# Revit family: Shower-Handshower-KOHLER-Awaken-K-99898
name_source: partatom
category: Plumbing Fixtures
revit_build: Autodesk Revit 2015 (Build: 20140606_1530(x64)
units: mm (PartAtom-declared; Revit-internal decimal feet)

## types (2) — shared parameters
ADA Compliant = Yes
Assembly Code = D2010700
CW Connection = Yes
Date Modified = 09/18/2017
Default Elevation = 42"
Description = G110 premium slidebar kit
Flow Rate = 2 GPM
HW Connection = Yes
Height = 46 9/16"
Length = 8 25/32"
Manufacturer = Kohler
MasterFormat 1995 = 15410
MasterFormat 2004 = 22.41.39
Material = Premium Metal
Pressure = 0.00 psi
Product Documentation Link = http://www.us.kohler.com
Product Name = Awaken
Product Page URL = http://www.us.kohler.com
URL = http://www.us.kohler.com
Width = 4 13/16"

## per-type parameters (varying)
| type | Finish | Model | Type |
| CP-Polished Chrome | Metal-Kohler-CP-Polished Chrome | K-99898-CP | 1 |
| BN-Vibrant Brushed Nickel | Metal-Kohler-BN-Vibrant Brushed Nickel | K-99898-BN | 2 |

## geometry (parser evidence)
native form markers: Sweep x6
no freeform markers — native parametric forms only
